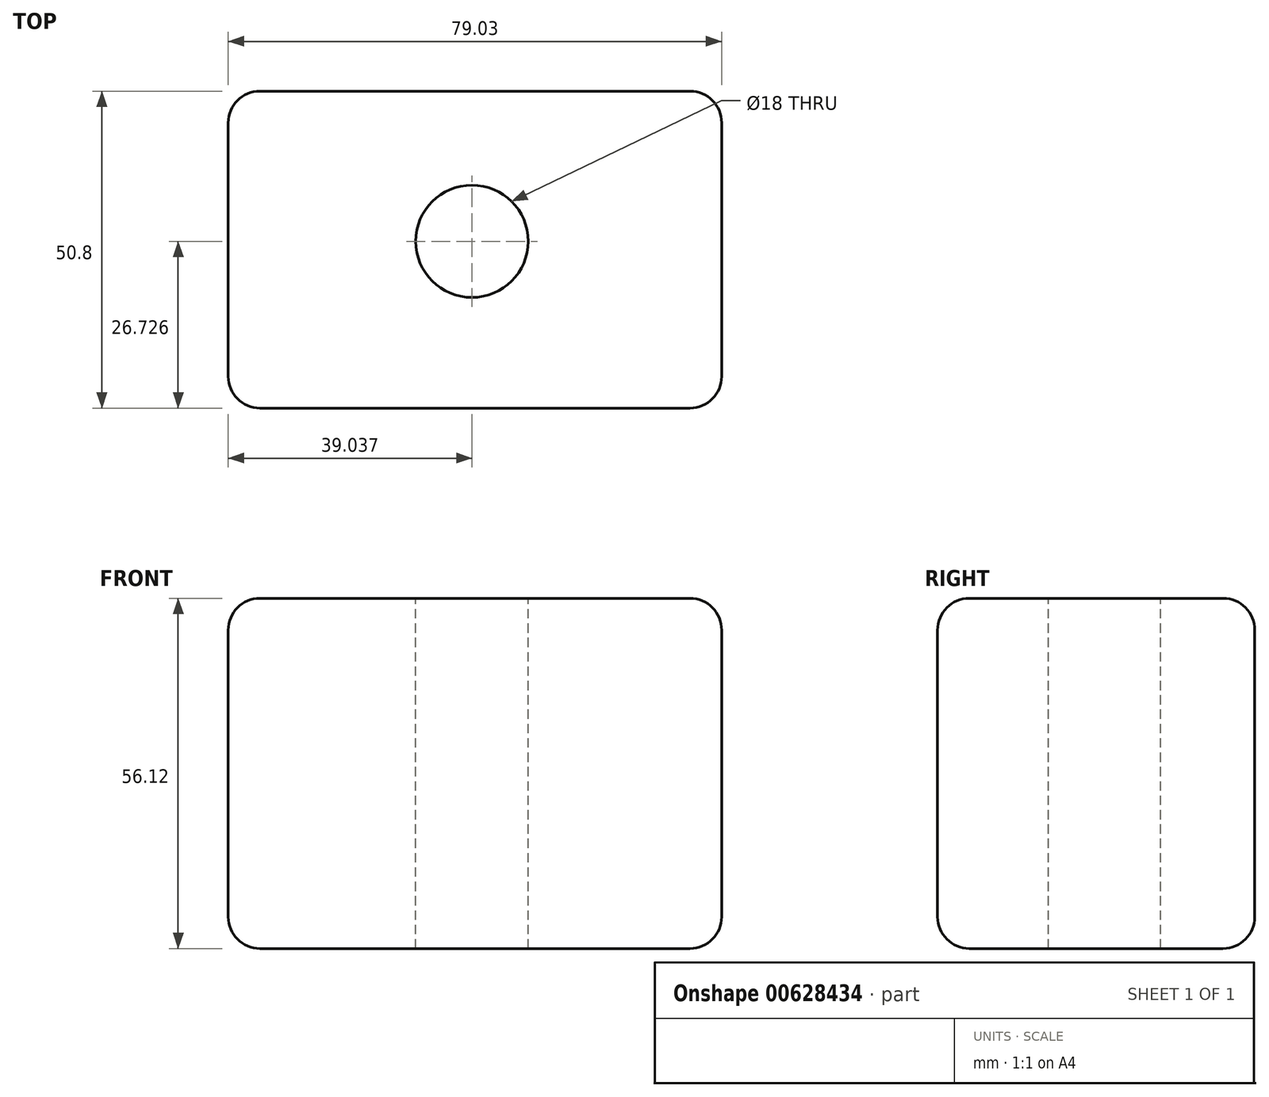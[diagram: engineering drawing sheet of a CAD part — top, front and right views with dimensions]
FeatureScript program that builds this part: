
annotation { "Feature Type Name" : "Feature", "Feature Type Description" : "" }
export const myFeature = defineFeature(function(context is Context, id is Id, definition is map)
    precondition{}
    {
        {
            var Q0;
            Q0=qCreatedBy(makeId("Front.planeOp"),FACE);
            var sketch = newSketch(context, id + "F0", { "sketchPlane" : qUnion([Q0])});
            skLineSegment(sketch, "E0.bottom", {"start": v(-29.41, 29.23) * mm, "end": v(49.62, 29.23) * mm});
            skLineSegment(sketch, "E0.top", {"start": v(-29.41, -26.89) * mm, "end": v(49.62, -26.89) * mm});
            skLineSegment(sketch, "E0.left", {"start": v(-29.41, 29.23) * mm, "end": v(-29.41, -26.89) * mm});
            skLineSegment(sketch, "E0.right", {"start": v(49.62, 29.23) * mm, "end": v(49.62, -26.89) * mm});
            skSolve(sketch);
        }
        {
            var Q0;
            Q0=makeQuery(id+"F0.imprint","IMPRINT",FACE,{"disambiguationData":[TD([[makeQuery(id+"F0.imprint","IMPRINT",EDGE,{"derivedFrom":sQuery(id+"F0.wireOp",EDGE,"E0.bottom")}),-1.0]])]});
            extrude(context, id + "F1", {"entities" : qUnion([Q0]), "depth" : 50.8 * mm, "offsetDistance" : 25.4 * mm});
        }
        {
            var Q0;
            Q0=makeQuery(id+"F1.opExtrude","CAP_EDGE",EDGE,{"disambiguationData":[OSD([sQuery(id+"F0.wireOp",EDGE,"E0.top")])],"isStart":false});
            var Q1;
            Q1=makeQuery(id+"F1.opExtrude","CAP_EDGE",EDGE,{"disambiguationData":[OSD([sQuery(id+"F0.wireOp",EDGE,"E0.left")])],"isStart":false});
            var Q2;
            Q2=makeQuery(id+"F1.opExtrude","CAP_EDGE",EDGE,{"disambiguationData":[OSD([sQuery(id+"F0.wireOp",EDGE,"E0.bottom")])],"isStart":false});
            var Q3;
            Q3=makeQuery(id+"F1.opExtrude","CAP_EDGE",EDGE,{"disambiguationData":[OSD([sQuery(id+"F0.wireOp",EDGE,"E0.right")])],"isStart":false});
            var Q4;
            Q4=makeQuery(id+"F1.opExtrude","SWEPT_EDGE",EDGE,{"disambiguationData":[OSD([sQuery(id+"F0.wireOp",EDGE,"E0.top"),sQuery(id+"F0.wireOp",EDGE,"E0.right")])]});
            var Q5;
            Q5=makeQuery(id+"F1.opExtrude","CAP_EDGE",EDGE,{"disambiguationData":[OSD([sQuery(id+"F0.wireOp",EDGE,"E0.top")])],"isStart":true});
            var Q6;
            Q6=makeQuery(id+"F1.opExtrude","SWEPT_EDGE",EDGE,{"disambiguationData":[OSD([sQuery(id+"F0.wireOp",EDGE,"E0.top"),sQuery(id+"F0.wireOp",EDGE,"E0.left")])]});
            var Q7;
            Q7=makeQuery(id+"F1.opExtrude","SWEPT_EDGE",EDGE,{"disambiguationData":[OSD([sQuery(id+"F0.wireOp",EDGE,"E0.bottom"),sQuery(id+"F0.wireOp",EDGE,"E0.right")])]});
            var Q8;
            Q8=makeQuery(id+"F1.opExtrude","CAP_FACE",FACE,{"disambiguationData":[OSD([sQuery(id+"F0.wireOp",EDGE,"E0.bottom"),sQuery(id+"F0.wireOp",EDGE,"E0.top"),sQuery(id+"F0.wireOp",EDGE,"E0.left"),sQuery(id+"F0.wireOp",EDGE,"E0.right")])],"isStart":true});
            var Q9;
            Q9=makeQuery(id+"F1.opExtrude","SWEPT_FACE",FACE,{"disambiguationData":[OSD([sQuery(id+"F0.wireOp",EDGE,"E0.left")])]});
            fillet(context, id + "F2", {"entities" : qUnion([Q0, Q1, Q2, Q3, Q4, Q5, Q6, Q7, Q8, Q9]), "radius" : 5.08 * mm, "tangentPropagation" : true, "allowEdgeOverflow" : false});
        }
        {
            var Q0;
            Q0=makeQuery(id+"F1.opExtrude","SWEPT_FACE",FACE,{"disambiguationData":[OSD([sQuery(id+"F0.wireOp",EDGE,"E0.bottom")])]});
            var sketch = newSketch(context, id + "F3", { "sketchPlane" : qUnion([Q0])});
            skCircle(sketch, "E1", {"center": v(9.63, -24.07) * mm, "radius": 9 * mm});
            skSolve(sketch);
        }
        {
            var Q0;
            Q0 = qSketchRegion(id + "F3", true);
            extrude(context, id + "F4", {"entities" : qUnion([Q0]), "operationType" : NewBodyOperationType.REMOVE, "endBound" : BoundingType.THROUGH_ALL, "oppositeDirection" : true, "depth" : 25.4 * mm, "offsetDistance" : 25.4 * mm});
        }
    });
